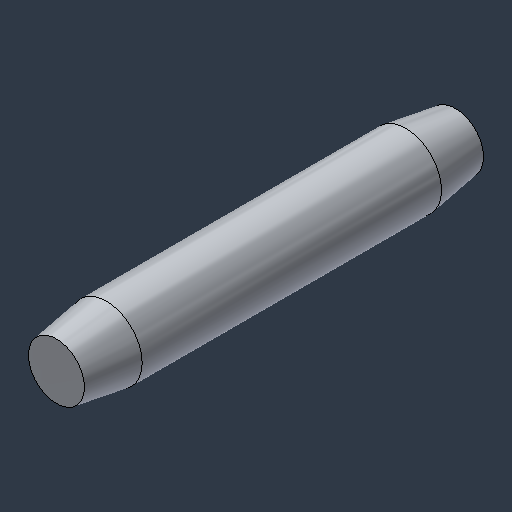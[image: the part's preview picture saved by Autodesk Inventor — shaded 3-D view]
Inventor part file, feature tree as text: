
AUTODESK INVENTOR PART (.ipt)
format: ipt  version: 2024.3 (Build 283343000, 343)  size: 105,472 bytes
history: native  units: mm (DEFAULTED — no unit token found)
features: chamfer x1
ambient origin geometry x8: Origin, YZ Plane, XZ Plane, XY Plane, X Axis, Y Axis, Z Axis, Center Point
bodies: Solid1 (feature_tree)
feature tree (1):
  chamfer  "Chamfer2"  [1 undecoded]
note: 1 required parameter value undecoded (feature->parameter linkage not recoverable at this tier; creation-order binding heuristic only, values carry confidence <= 0.55)
